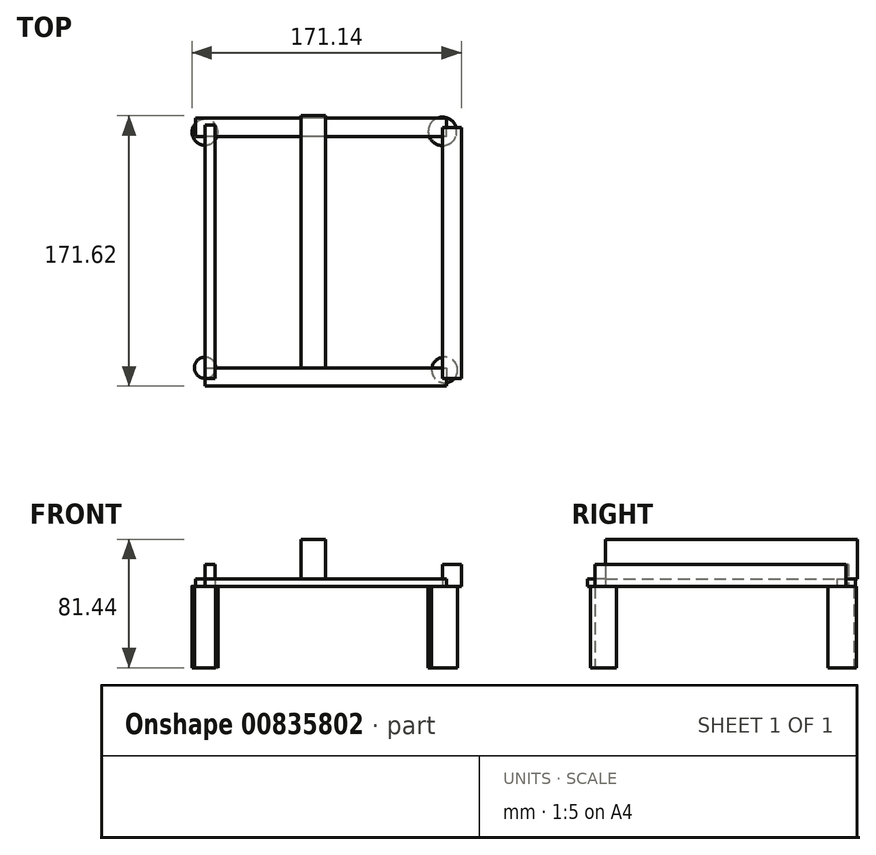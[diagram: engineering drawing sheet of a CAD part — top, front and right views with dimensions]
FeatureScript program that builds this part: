
annotation { "Feature Type Name" : "Feature", "Feature Type Description" : "" }
export const myFeature = defineFeature(function(context is Context, id is Id, definition is map)
    precondition{}
    {
        {
            var Q0;
            Q0=qCreatedBy(makeId("Top.planeOp"),FACE);
            var sketch = newSketch(context, id + "F0", { "sketchPlane" : qUnion([Q0])});
            skCircle(sketch, "E0", {"center": v(-76.1, -74.49) * mm, "radius": 6.75 * mm});
            skCircle(sketch, "E1", {"center": v(-76.2, 75.13) * mm, "radius": 8.24 * mm});
            skCircle(sketch, "E2", {"center": v(76.05, -75.91) * mm, "radius": 8.2 * mm});
            skCircle(sketch, "E3", {"center": v(74.7, 75.67) * mm, "radius": 9.05 * mm});
            skSolve(sketch);
        }
        {
            var Q0;
            Q0 = qSketchRegion(id + "F0", true);
            extrude(context, id + "F1", {"entities" : qUnion([Q0]), "depth" : 51.63 * mm, "offsetDistance" : 25 * mm});
        }
        {
            var Q0;
            Q0=makeQuery(id+"F1.opExtrude","CAP_FACE",FACE,{"disambiguationData":[OSD([sQuery(id+"F0.wireOp",EDGE,"E0")])],"isStart":false});
            var sketch = newSketch(context, id + "F2", { "sketchPlane" : qUnion([Q0])});
            skLineSegment(sketch, "E4.bottom", {"start": v(-76.1, -74.49) * mm, "end": v(77.1, -74.49) * mm});
            skLineSegment(sketch, "E4.top", {"start": v(-76.1, -86.07) * mm, "end": v(77.1, -86.07) * mm});
            skLineSegment(sketch, "E4.left", {"start": v(-76.1, -74.49) * mm, "end": v(-76.1, -86.07) * mm});
            skLineSegment(sketch, "E4.right", {"start": v(77.1, -74.49) * mm, "end": v(77.1, -86.07) * mm});
            skLineSegment(sketch, "E5.bottom", {"start": v(77.1, 72.37) * mm, "end": v(-82.08, 72.37) * mm});
            skLineSegment(sketch, "E5.top", {"start": v(77.1, 84.24) * mm, "end": v(-82.08, 84.24) * mm});
            skLineSegment(sketch, "E5.left", {"start": v(77.1, 72.37) * mm, "end": v(77.1, 84.24) * mm});
            skLineSegment(sketch, "E5.right", {"start": v(-82.08, 72.37) * mm, "end": v(-82.08, 84.24) * mm});
            skSolve(sketch);
        }
        {
            var Q0;
            Q0 = qSketchRegion(id + "F2", true);
            extrude(context, id + "F3", {"entities" : qUnion([Q0]), "depth" : 4.8 * mm, "offsetDistance" : 25 * mm});
        }
        {
            var Q0;
            Q0=makeQuery(id+"F1.opExtrude","CAP_FACE",FACE,{"disambiguationData":[OSD([sQuery(id+"F0.wireOp",EDGE,"E0")])],"isStart":false});
            var sketch = newSketch(context, id + "F4", { "sketchPlane" : qUnion([Q0])});
            skLineSegment(sketch, "E6.bottom", {"start": v(-69.68, 79.64) * mm, "end": v(-76.1, 79.64) * mm});
            skLineSegment(sketch, "E6.top", {"start": v(-69.68, -81.24) * mm, "end": v(-76.1, -81.24) * mm});
            skLineSegment(sketch, "E6.left", {"start": v(-69.68, 79.64) * mm, "end": v(-69.68, -81.24) * mm});
            skLineSegment(sketch, "E6.right", {"start": v(-76.1, 79.64) * mm, "end": v(-76.1, -81.24) * mm});
            skLineSegment(sketch, "E7.bottom", {"start": v(86.7, 78.16) * mm, "end": v(74.66, 78.16) * mm});
            skLineSegment(sketch, "E7.top", {"start": v(86.7, -81.24) * mm, "end": v(74.66, -81.24) * mm});
            skLineSegment(sketch, "E7.left", {"start": v(86.7, 78.16) * mm, "end": v(86.7, -81.24) * mm});
            skLineSegment(sketch, "E7.right", {"start": v(74.66, 78.16) * mm, "end": v(74.66, -81.24) * mm});
            skSolve(sketch);
        }
        {
            var Q0;
            Q0 = qSketchRegion(id + "F4", true);
            extrude(context, id + "F5", {"entities" : qUnion([Q0]), "depth" : 13.88 * mm, "offsetDistance" : 25 * mm});
        }
        {
            var Q0;
            Q0=makeQuery(id+"F3.opExtrude","CAP_FACE",FACE,{"disambiguationData":[OSD([sQuery(id+"F2.wireOp",EDGE,"E4.bottom"),sQuery(id+"F2.wireOp",EDGE,"E4.top"),sQuery(id+"F2.wireOp",EDGE,"E4.left"),sQuery(id+"F2.wireOp",EDGE,"E4.right")])],"isStart":false});
            var sketch = newSketch(context, id + "F6", { "sketchPlane" : qUnion([Q0])});
            skLineSegment(sketch, "E8.bottom", {"start": v(0.5, -86.07) * mm, "end": v(-15.2, -86.07) * mm});
            skLineSegment(sketch, "E8.top", {"start": v(0.5, 85.55) * mm, "end": v(-15.2, 85.55) * mm});
            skLineSegment(sketch, "E8.left", {"start": v(0.5, -86.07) * mm, "end": v(0.5, 85.55) * mm});
            skLineSegment(sketch, "E8.right", {"start": v(-15.2, -86.07) * mm, "end": v(-15.2, 85.55) * mm});
            skSolve(sketch);
        }
        {
            var Q0;
            {var subQ0=sQuery(id+"F6.wireOp",EDGE,"E8.top");Q0=makeQuery(id+"F6.imprint","IMPRINT",FACE,{"disambiguationData":[TD([[makeQuery(id+"F6.imprint","IMPRINT",EDGE,{"derivedFrom":subQ0}),1.0]])]});}
            extrude(context, id + "F7", {"entities" : qUnion([Q0]), "operationType" : NewBodyOperationType.ADD, "depth" : 25 * mm, "offsetDistance" : 25 * mm});
        }
    });
